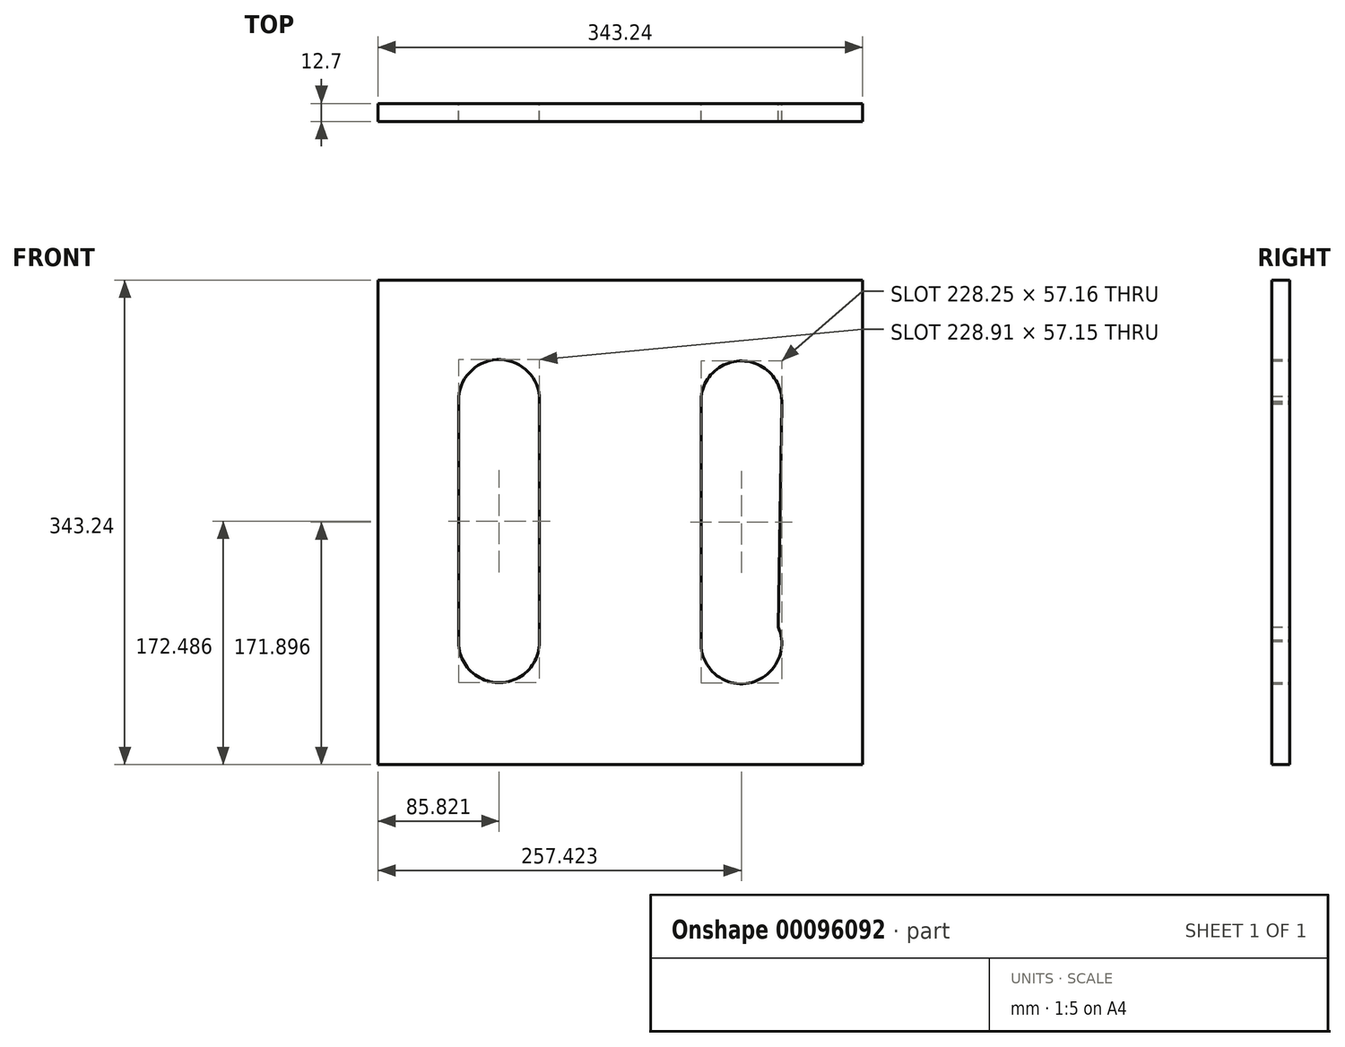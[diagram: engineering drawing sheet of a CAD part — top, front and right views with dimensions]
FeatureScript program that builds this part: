
annotation { "Feature Type Name" : "Feature", "Feature Type Description" : "" }
export const myFeature = defineFeature(function(context is Context, id is Id, definition is map)
    precondition{}
    {
        {
            var Q0;
            Q0=qCreatedBy(makeId("Front.planeOp"),FACE);
            var sketch = newSketch(context, id + "F0", { "sketchPlane" : qUnion([Q0])});
            skLineSegment(sketch, "E0.bottom", {"start": v(-171.62, -171.62) * mm, "end": v(171.62, -171.62) * mm});
            skLineSegment(sketch, "E0.top", {"start": v(-171.62, 171.62) * mm, "end": v(171.62, 171.62) * mm});
            skLineSegment(sketch, "E0.left", {"start": v(-171.62, -171.62) * mm, "end": v(-171.62, 171.62) * mm});
            skLineSegment(sketch, "E0.right", {"start": v(171.62, -171.62) * mm, "end": v(171.62, 171.62) * mm});
            skPoint(sketch, "E0.middle", {"position": v(0, 0) * mm});
            skArc(sketch, "E1", {"start": v(-57.3, 89.39) * mm, "mid": v(-87.5, 115.32) * mm, "end": v(-114.37, 85.94) * mm});
            skArc(sketch, "E2", {"start": v(114.37, 84.17) * mm, "mid": v(86.29, 114.4) * mm, "end": v(57.22, 85.1) * mm});
            skArc(sketch, "E3", {"start": v(57.22, -84.35) * mm, "mid": v(91.05, -113.85) * mm, "end": v(111.93, -74.12) * mm});
            skArc(sketch, "E4", {"start": v(-114.37, -83.22) * mm, "mid": v(-86.7, -113.59) * mm, "end": v(-57.22, -84.99) * mm});
            skLineSegment(sketch, "E5", {"start": v(-114.37, 87.6) * mm, "end": v(-114.37, -86.77) * mm});
            skLineSegment(sketch, "E6", {"start": v(-57.3, 89.39) * mm, "end": v(-57.22, -84.99) * mm});
            skLineSegment(sketch, "E7", {"start": v(57.22, 86.5) * mm, "end": v(57.22, -87.13) * mm});
            skLineSegment(sketch, "E8", {"start": v(114.41, 86.55) * mm, "end": v(111.56, -98.15) * mm});
            skSolve(sketch);
        }
        {
            var Q0;
            Q0=makeQuery(id+"F0.imprint","IMPRINT",FACE,{"disambiguationData":[TD([[makeQuery(id+"F0.imprint","IMPRINT",EDGE,{"derivedFrom":sQuery(id+"F0.wireOp",EDGE,"E0.bottom")}),1.0]])]});
            extrude(context, id + "F1", {"entities" : qUnion([Q0]), "depth" : 12.7 * mm});
        }
    });
